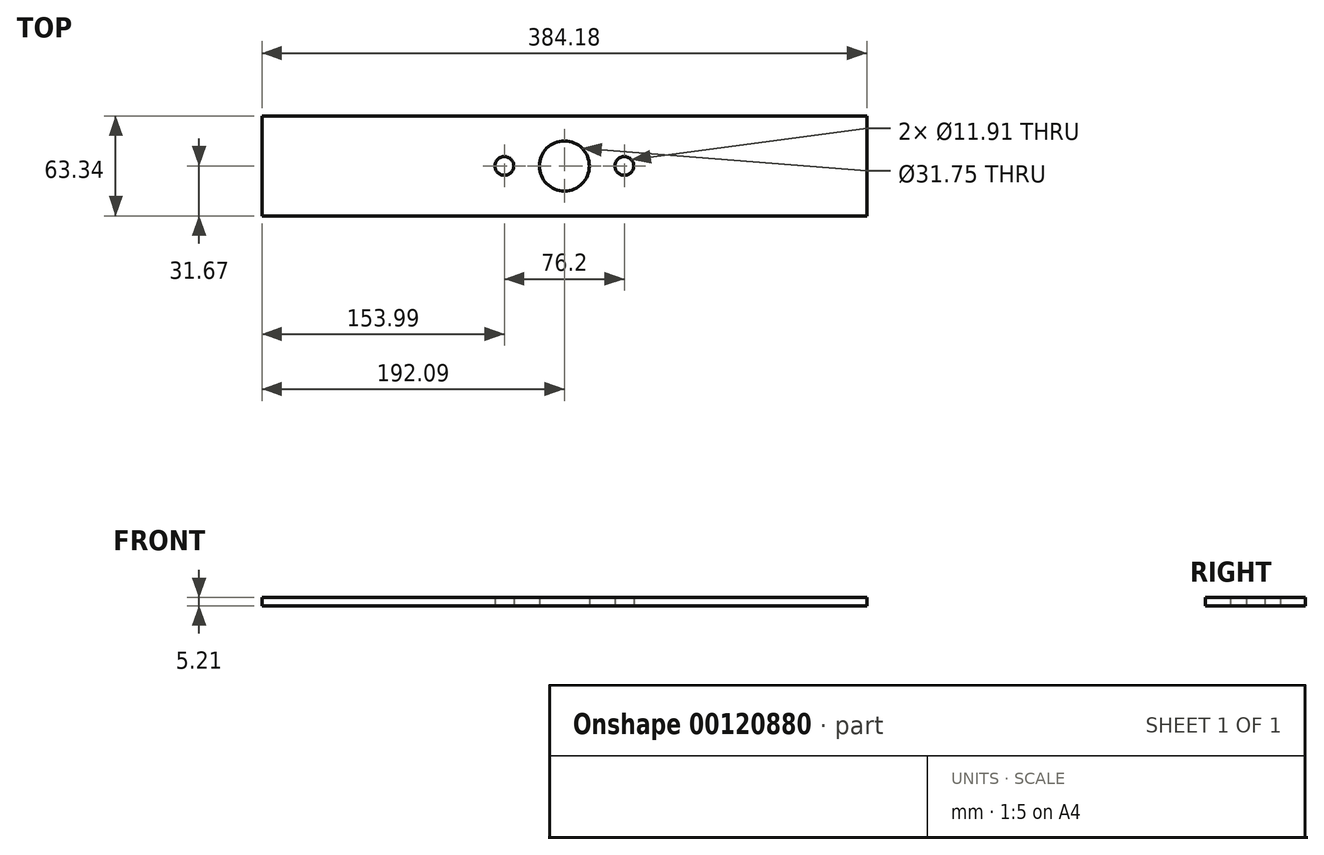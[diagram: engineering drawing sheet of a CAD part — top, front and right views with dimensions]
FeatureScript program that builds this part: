
annotation { "Feature Type Name" : "Feature", "Feature Type Description" : "" }
export const myFeature = defineFeature(function(context is Context, id is Id, definition is map)
    precondition{}
    {
        {
            var Q0;
            Q0=qCreatedBy(makeId("Top.planeOp"),FACE);
            var sketch = newSketch(context, id + "F0", { "sketchPlane" : qUnion([Q0])});
            skLineSegment(sketch, "E0.bottom", {"start": v(-192.09, 31.67) * mm, "end": v(192.09, 31.67) * mm});
            skLineSegment(sketch, "E0.top", {"start": v(-192.09, -31.67) * mm, "end": v(192.09, -31.67) * mm});
            skLineSegment(sketch, "E0.left", {"start": v(-192.09, 31.67) * mm, "end": v(-192.09, -31.67) * mm});
            skLineSegment(sketch, "E0.right", {"start": v(192.09, 31.67) * mm, "end": v(192.09, -31.67) * mm});
            skPoint(sketch, "E0.middle", {"position": v(0, 0) * mm});
            skCircle(sketch, "E1", {"center": v(0, 0) * mm, "radius": 15.88 * mm});
            skCircle(sketch, "E2", {"center": v(-38.1, 0) * mm, "radius": 5.96 * mm});
            skCircle(sketch, "E3.MirrorC", {"center": v(38.1, 0) * mm, "radius": 5.96 * mm});
            skSolve(sketch);
        }
        {
            var Q0;
            Q0 = qSketchRegion(id + "F0", true);
            extrude(context, id + "F1", {"entities" : qUnion([Q0]), "depth" : 5.2 * mm});
        }
    });
